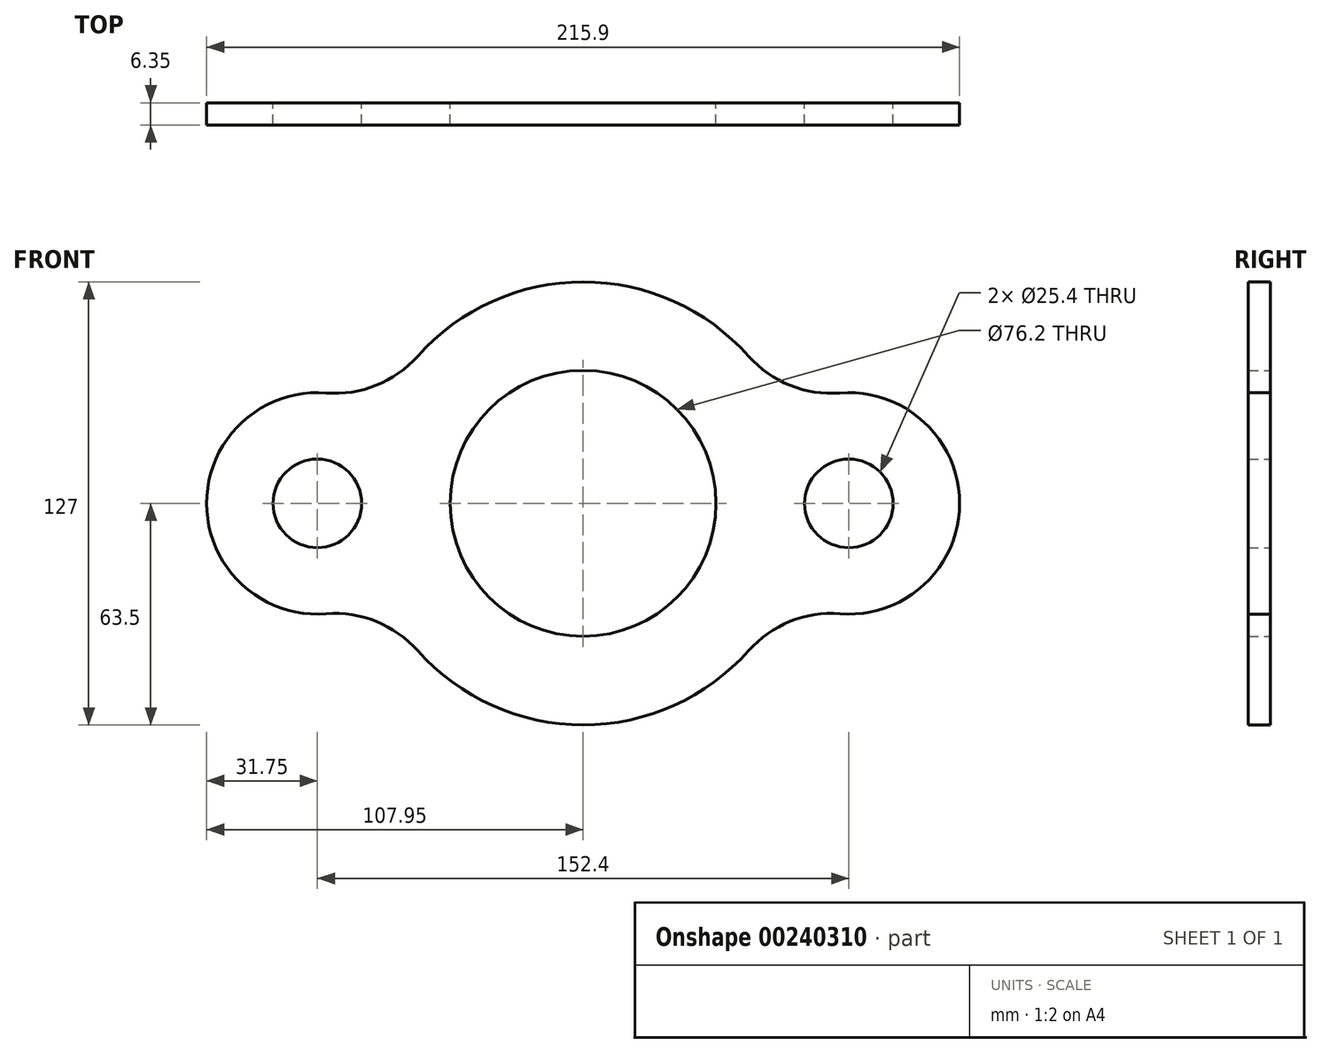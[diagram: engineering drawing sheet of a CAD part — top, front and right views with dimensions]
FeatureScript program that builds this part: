
annotation { "Feature Type Name" : "Feature", "Feature Type Description" : "" }
export const myFeature = defineFeature(function(context is Context, id is Id, definition is map)
    precondition{}
    {
        {
            var Q0;
            Q0=qCreatedBy(makeId("Front.planeOp"),FACE);
            var sketch = newSketch(context, id + "F0", { "sketchPlane" : qUnion([Q0])});
            skCircle(sketch, "E0", {"center": v(-76.2, 0) * mm, "radius": 12.7 * mm});
            skArc(sketch, "E1", {"start": v(-73.69, 31.65) * mm, "mid": v(-107.95, 0) * mm, "end": v(-73.69, -31.65) * mm});
            skCircle(sketch, "E2", {"center": v(76.2, 0) * mm, "radius": 12.7 * mm});
            skArc(sketch, "E3", {"start": v(73.69, -31.65) * mm, "mid": v(107.95, 0) * mm, "end": v(73.69, 31.65) * mm});
            skArc(sketch, "E4", {"start": v(-47.45, -42.2) * mm, "mid": v(0, -63.5) * mm, "end": v(47.45, -42.2) * mm});
            skCircle(sketch, "E5", {"center": v(0, 0) * mm, "radius": 38.1 * mm});
            skArc(sketch, "E6.trimOffspring", {"start": v(47.45, 42.2) * mm, "mid": v(0, 63.5) * mm, "end": v(-47.45, 42.2) * mm});
            skPoint(sketch, "E7.visualSharp", {"position": v(-57.94, 25.98) * mm});
            skArc(sketch, "E7.filletArc", {"start": v(-73.69, 31.65) * mm, "mid": v(-59.33, 33.84) * mm, "end": v(-47.45, 42.2) * mm});
            skPoint(sketch, "E8.visualSharp", {"position": v(-57.94, -25.98) * mm});
            skArc(sketch, "E8.filletArc", {"start": v(-47.45, -42.2) * mm, "mid": v(-59.33, -33.84) * mm, "end": v(-73.69, -31.65) * mm});
            skPoint(sketch, "E9.visualSharp", {"position": v(57.94, 25.98) * mm});
            skArc(sketch, "E9.filletArc", {"start": v(47.45, 42.2) * mm, "mid": v(59.33, 33.84) * mm, "end": v(73.69, 31.65) * mm});
            skPoint(sketch, "E10.visualSharp", {"position": v(57.94, -25.98) * mm});
            skArc(sketch, "E10.filletArc", {"start": v(73.69, -31.65) * mm, "mid": v(59.33, -33.84) * mm, "end": v(47.45, -42.2) * mm});
            skLineSegment(sketch, "E11", {"start": v(76.2, 0) * mm, "end": v(0, 0) * mm, "construction": true});
            skLineSegment(sketch, "E12", {"start": v(-76.2, 0) * mm, "end": v(0, 0) * mm, "construction": true});
            skSolve(sketch);
        }
        {
            var Q0;
            Q0=makeQuery(id+"F0.imprint","IMPRINT",FACE,{"disambiguationData":[TD([[makeQuery(id+"F0.imprint","IMPRINT",EDGE,{"derivedFrom":sQuery(id+"F0.wireOp",EDGE,"E0")}),-1.0]])]});
            extrude(context, id + "F1", {"entities" : qUnion([Q0]), "depth" : 6.35 * mm});
        }
    });
